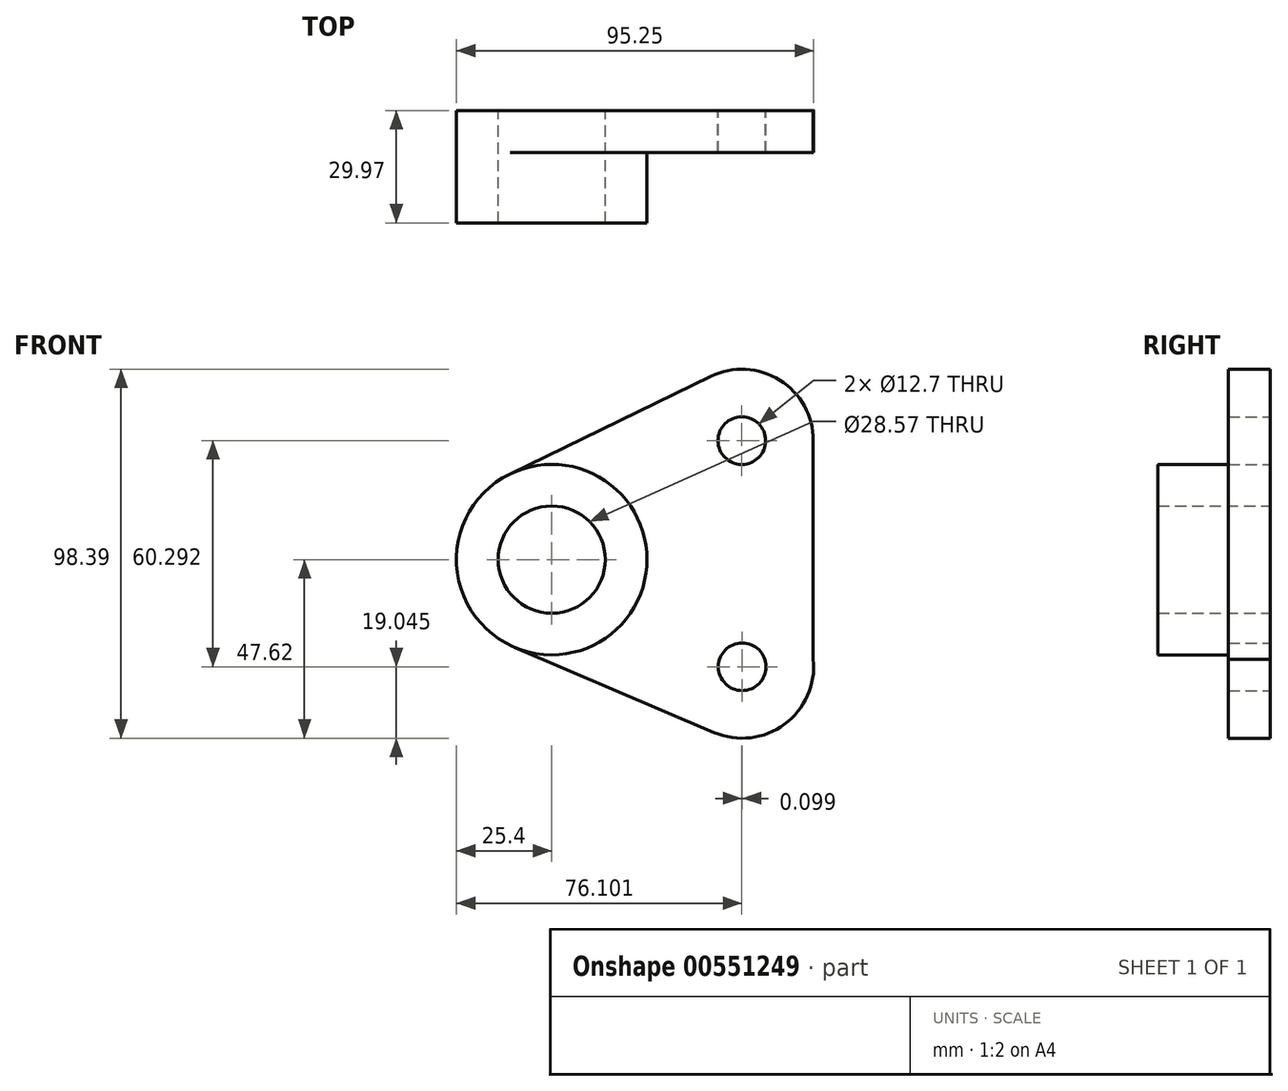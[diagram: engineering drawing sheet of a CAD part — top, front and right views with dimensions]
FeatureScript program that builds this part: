
annotation { "Feature Type Name" : "Feature", "Feature Type Description" : "" }
export const myFeature = defineFeature(function(context is Context, id is Id, definition is map)
    precondition{}
    {
        {
            var Q0;
            Q0=qCreatedBy(makeId("Front.planeOp"),FACE);
            var sketch = newSketch(context, id + "F0", { "sketchPlane" : qUnion([Q0])});
            skCircle(sketch, "E0", {"center": v(0, 0) * mm, "radius": 25.4 * mm});
            skArc(sketch, "E1", {"start": v(69.75, 31.72) * mm, "mid": v(60.8, 47.87) * mm, "end": v(42.37, 48.85) * mm});
            skLineSegment(sketch, "E2", {"start": v(-11.1, 22.84) * mm, "end": v(43.06, 49.18) * mm});
            skLineSegment(sketch, "E3", {"start": v(-9.97, -23.36) * mm, "end": v(45.43, -47) * mm});
            skLineSegment(sketch, "E4", {"start": v(69.75, -26.63) * mm, "end": v(69.75, 31.72) * mm});
            skCircle(sketch, "E5", {"center": v(50.7, 31.72) * mm, "radius": 6.35 * mm});
            skCircle(sketch, "E6", {"center": v(50.8, -28.57) * mm, "radius": 6.35 * mm});
            skArc(sketch, "E7", {"start": v(43.33, -46.1) * mm, "mid": v(62.1, -43.91) * mm, "end": v(69.75, -26.63) * mm});
            skCircle(sketch, "E8", {"center": v(0, 0) * mm, "radius": 14.29 * mm});
            skSolve(sketch);
        }
        {
            var Q0;
            Q0 = qSketchRegion(id + "F0", true);
            extrude(context, id + "F1", {"entities" : qUnion([Q0]), "depth" : 11.18 * mm, "offsetDistance" : 25.4 * mm});
        }
        {
            var Q0;
            Q0=makeQuery(id+"F0.imprint","IMPRINT",FACE,{"disambiguationData":[TD([[makeQuery(id+"F0.imprint","IMPRINT",EDGE,{"derivedFrom":sQuery(id+"F0.wireOp",EDGE,"E8")}),-1.0]])]});
            extrude(context, id + "F2", {"entities" : qUnion([Q0]), "operationType" : NewBodyOperationType.ADD, "depth" : 29.97 * mm, "offsetDistance" : 25.4 * mm});
        }
    });
